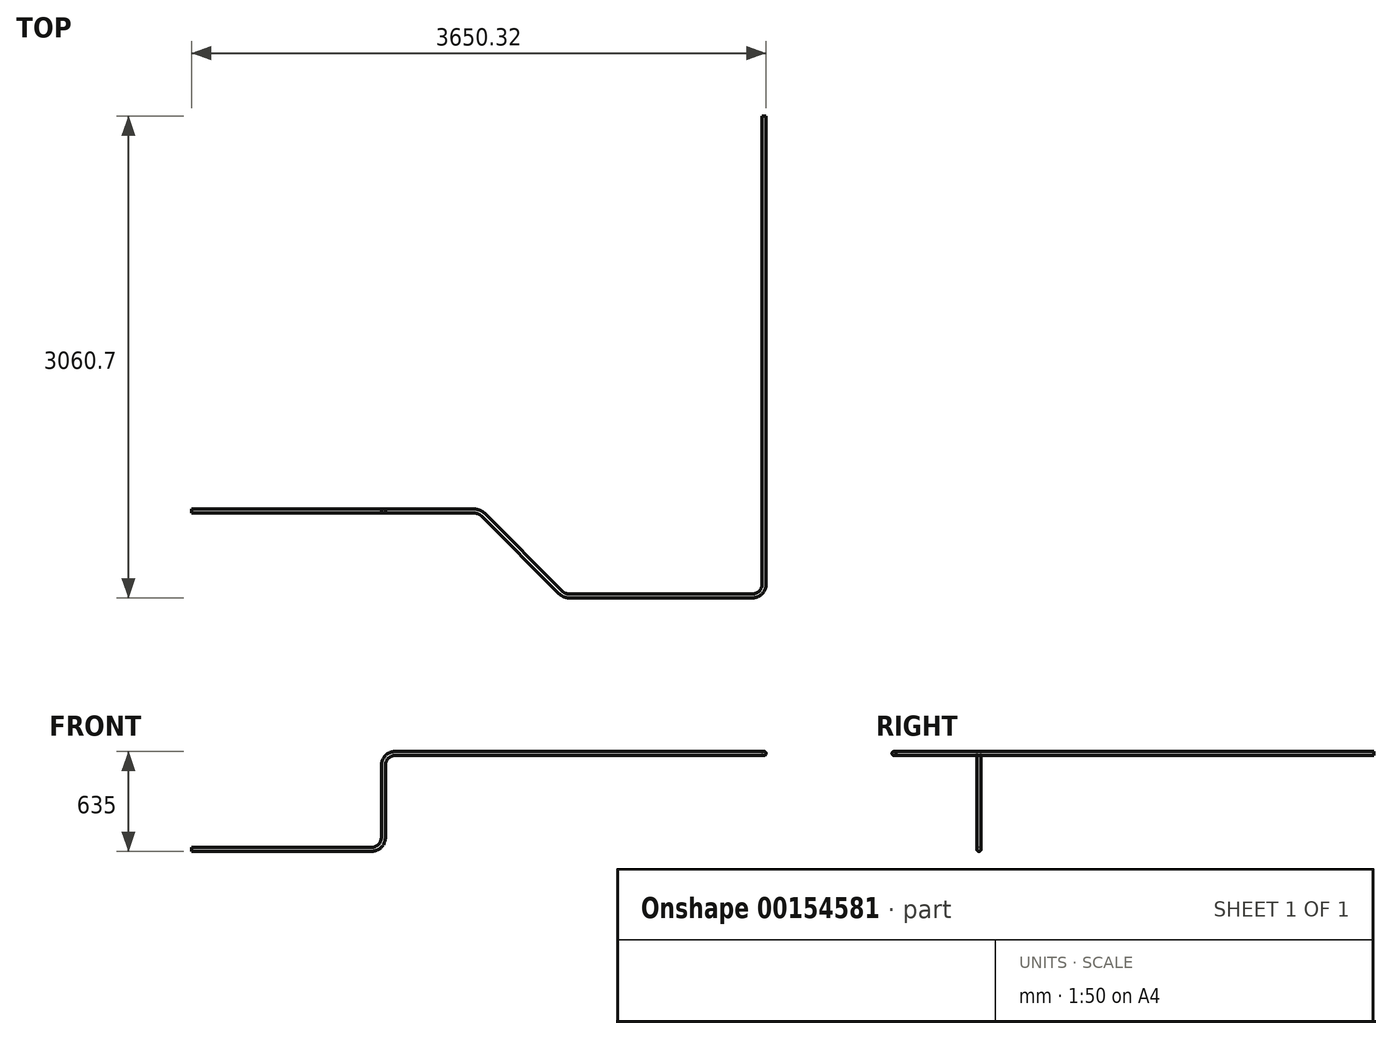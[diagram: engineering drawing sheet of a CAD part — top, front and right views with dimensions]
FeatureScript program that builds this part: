
annotation { "Feature Type Name" : "Feature", "Feature Type Description" : "" }
export const myFeature = defineFeature(function(context is Context, id is Id, definition is map)
    precondition{}
    {
        {
            var Q0;
            Q0=qCreatedBy(makeId("Front.planeOp"),FACE);
            var sketch = newSketch(context, id + "F0", { "sketchPlane" : qUnion([Q0])});
            skLineSegment(sketch, "E0", {"start": v(0, 0) * mm, "end": v(1143, 0) * mm});
            skLineSegment(sketch, "E1", {"start": v(1219.2, 76.2) * mm, "end": v(1219.2, 533.4) * mm});
            skPoint(sketch, "E2.visualSharp", {"position": v(1219.2, 0) * mm});
            skArc(sketch, "E2.filletArc", {"start": v(1143, 0) * mm, "mid": v(1196.88, 22.32) * mm, "end": v(1219.2, 76.2) * mm});
            skPoint(sketch, "E3.visualSharp", {"position": v(1219.2, 609.6) * mm});
            skArc(sketch, "E3.filletArc", {"start": v(1295.4, 609.6) * mm, "mid": v(1241.52, 587.28) * mm, "end": v(1219.2, 533.4) * mm});
            skPoint(sketch, "E4.end.orphan", {"position": v(1828.8, 609.6) * mm});
            skSolve(sketch);
        }
        {
            var Q0;
            Q0=qCreatedBy(makeId("Top.planeOp"),FACE);
            cPlane(context, id + "F1", {"entities" : qUnion([Q0]), "cplaneType" : CPlaneType.OFFSET, "offset" : 609.6 * mm, "width" : 152.4 * mm, "height" : 152.4 * mm});
        }
        {
            var Q0;
            Q0=qCreatedBy(id+"F1.planeOp",FACE);
            var sketch = newSketch(context, id + "F2", { "sketchPlane" : qUnion([Q0])});
            skLineSegment(sketch, "E5", {"start": v(1851.12, -22.32) * mm, "end": v(2345.3, -516.5) * mm});
            skLineSegment(sketch, "E6", {"start": v(2399.18, -538.82) * mm, "end": v(3561.42, -538.82) * mm});
            skLineSegment(sketch, "E7", {"start": v(3637.62, -462.62) * mm, "end": v(3637.62, 2509.18) * mm});
            skPoint(sketch, "E8.visualSharp", {"position": v(2367.62, -538.82) * mm});
            skArc(sketch, "E8.filletArc", {"start": v(2345.3, -516.5) * mm, "mid": v(2370.02, -533.01) * mm, "end": v(2399.18, -538.82) * mm});
            skPoint(sketch, "E9.visualSharp", {"position": v(3637.62, -538.82) * mm});
            skArc(sketch, "E9.filletArc", {"start": v(3561.42, -538.82) * mm, "mid": v(3615.3, -516.5) * mm, "end": v(3637.62, -462.62) * mm});
            skArc(sketch, "E10.filletArc", {"start": v(1851.12, -22.32) * mm, "mid": v(1826.4, -5.8) * mm, "end": v(1797.24, 0) * mm});
            skLineSegment(sketch, "E11", {"start": v(1797.24, 0) * mm, "end": v(1295.4, 0) * mm});
            skLineSegment(sketch, "E12", {"start": v(3637.62, 677.7) * mm, "end": v(2804.24, 677.7) * mm});
            skLineSegment(sketch, "E13", {"start": v(3637.62, 1177.51) * mm, "end": v(2804.24, 1177.51) * mm});
            skSolve(sketch);
        }
        {
            var Q0;
            Q0=qCreatedBy(makeId("Right.planeOp"),FACE);
            var sketch = newSketch(context, id + "F4", { "sketchPlane" : qUnion([Q0])});
            skCircle(sketch, "E14", {"center": v(0, 0) * mm, "radius": 12.7 * mm});
            skSolve(sketch);
        }
        {
            var Q0;
            Q0 = qSketchRegion(id + "F4", true);
            var Q1;
            Q1=sQuery(id+"F0.wireOp",EDGE,"E0");
            var Q2;
            Q2=sQuery(id+"F0.wireOp",EDGE,"E2.filletArc");
            var Q3;
            Q3=sQuery(id+"F0.wireOp",EDGE,"E1");
            var Q4;
            Q4=sQuery(id+"F0.wireOp",EDGE,"E3.filletArc");
            var Q5;
            Q5=sQuery(id+"F0.wireOp",EDGE,"E4");
            var Q6;
            Q6=sQuery(id+"F2.wireOp",EDGE,"E5");
            var Q7;
            Q7=sQuery(id+"F2.wireOp",EDGE,"E6");
            var Q8;
            Q8=sQuery(id+"F2.wireOp",EDGE,"E7");
            var Q9;
            Q9=sQuery(id+"F2.wireOp",EDGE,"E8.filletArc");
            var Q10;
            Q10=sQuery(id+"F2.wireOp",EDGE,"E9.filletArc");
            var Q11;
            Q11=sQuery(id+"F2.wireOp",EDGE,"E10.filletArc");
            var Q12;
            Q12=sQuery(id+"F2.wireOp",EDGE,"E11");
            sweep(context, id + "F3", {"profiles" : qUnion([Q0]), "path" : qUnion([Q1, Q2, Q3, Q4, Q5, Q6, Q7, Q8, Q9, Q10, Q11, Q12])});
        }
    });
